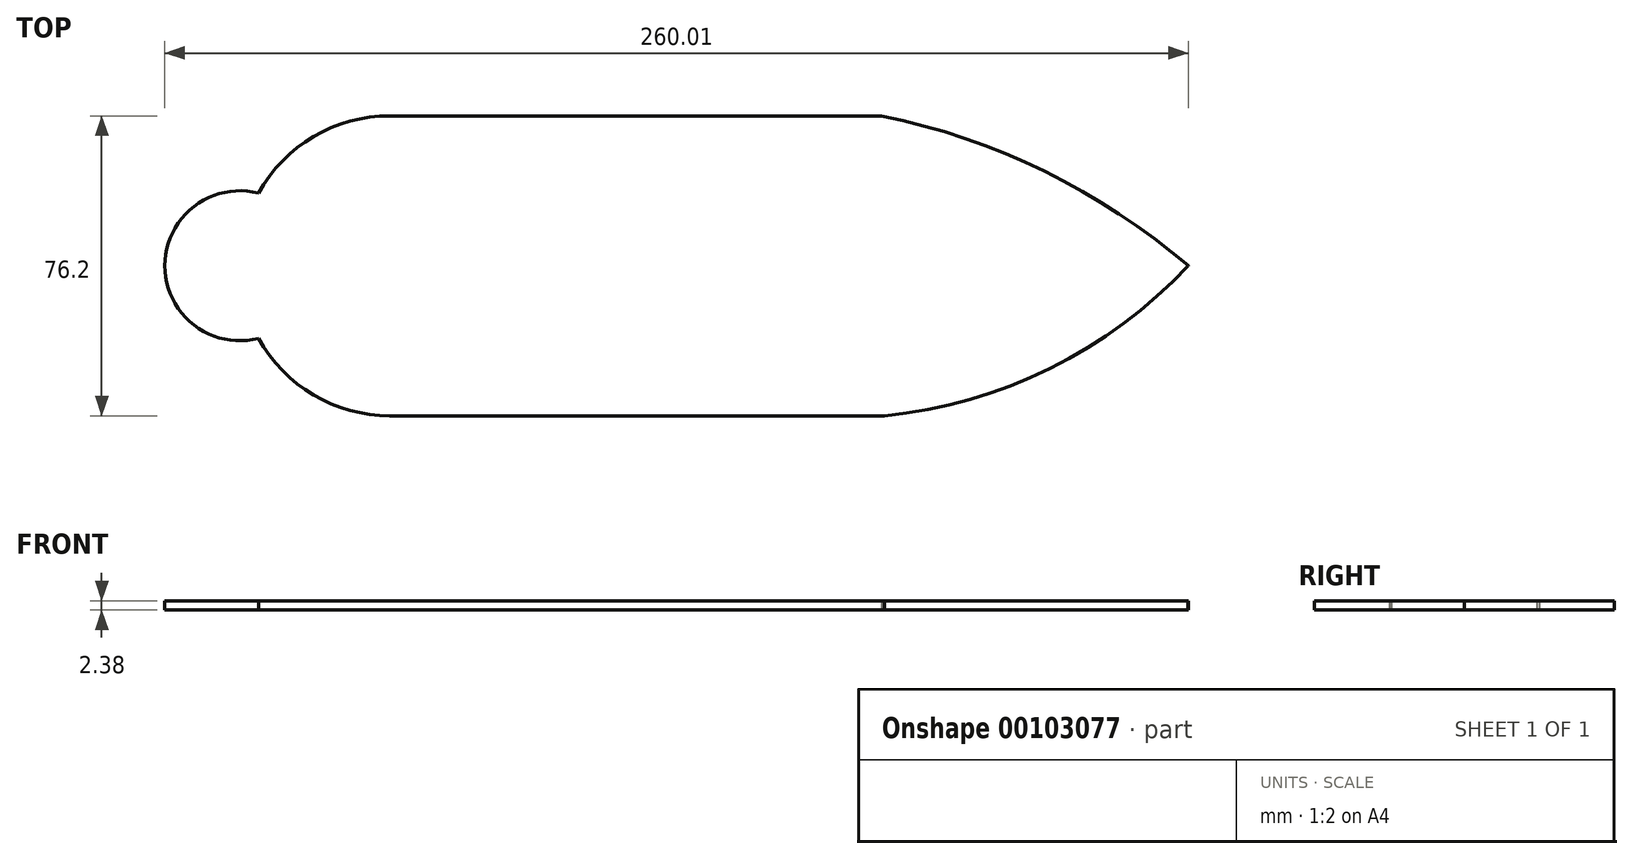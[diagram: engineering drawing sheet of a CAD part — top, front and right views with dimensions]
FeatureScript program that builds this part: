
annotation { "Feature Type Name" : "Feature", "Feature Type Description" : "" }
export const myFeature = defineFeature(function(context is Context, id is Id, definition is map)
    precondition{}
    {
        {
            var Q0;
            Q0=qCreatedBy(makeId("Top.planeOp"),FACE);
            var sketch = newSketch(context, id + "F0", { "sketchPlane" : qUnion([Q0])});
            skArc(sketch, "E0", {"start": v(-49.1, 18.45) * mm, "mid": v(-72.92, 0) * mm, "end": v(-49.1, -18.45) * mm});
            skArc(sketch, "E1", {"start": v(-49.1, -18.45) * mm, "mid": v(-35.12, -32.82) * mm, "end": v(-15.77, -38.1) * mm});
            skPoint(sketch, "E2.start.orphan", {"position": v(-72.92, 0) * mm});
            skLineSegment(sketch, "E3", {"start": v(-15.77, 38.1) * mm, "end": v(109.18, 38.1) * mm});
            skLineSegment(sketch, "E4", {"start": v(-15.77, -38.1) * mm, "end": v(109.95, -38.1) * mm});
            skLineSegment(sketch, "E5", {"start": v(187.06, 0) * mm, "end": v(187.43, 0) * mm});
            skLineSegment(sketch, "E6.bottom", {"start": v(187.06, 0) * mm, "end": v(187.09, 0) * mm});
            skArc(sketch, "E7.trimOffspring", {"start": v(187.09, 0) * mm, "mid": v(150.56, 24) * mm, "end": v(109.18, 38.1) * mm});
            skPoint(sketch, "E8.orphan", {"position": v(111.23, 38.1) * mm});
            skArc(sketch, "E9", {"start": v(-14.77, 38.1) * mm, "mid": v(-14.76, 38.1) * mm, "end": v(-14.76, 38.09) * mm});
            skArc(sketch, "E10.trimOffspring", {"start": v(109.95, -38.1) * mm, "mid": v(152, -26.1) * mm, "end": v(187.07, 0.01) * mm});
            skPoint(sketch, "E11.orphan", {"position": v(111.23, -38.1) * mm});
            skArc(sketch, "E12.trimOffspring", {"start": v(-14.76, 38.09) * mm, "mid": v(-34.68, 33.07) * mm, "end": v(-49.1, 18.45) * mm});
            skPoint(sketch, "E13.end.orphan", {"position": v(187.43, -47.02) * mm});
            skArc(sketch, "E14", {"start": v(-49.1, 18.45) * mm, "mid": v(-53.91, 0) * mm, "end": v(-49.1, -18.45) * mm});
            skSolve(sketch);
        }
        {
            var Q0;
            Q0 = qSketchRegion(id + "F0", true);
            extrude(context, id + "F1", {"entities" : qUnion([Q0]), "depth" : 2.38 * mm});
        }
    });
